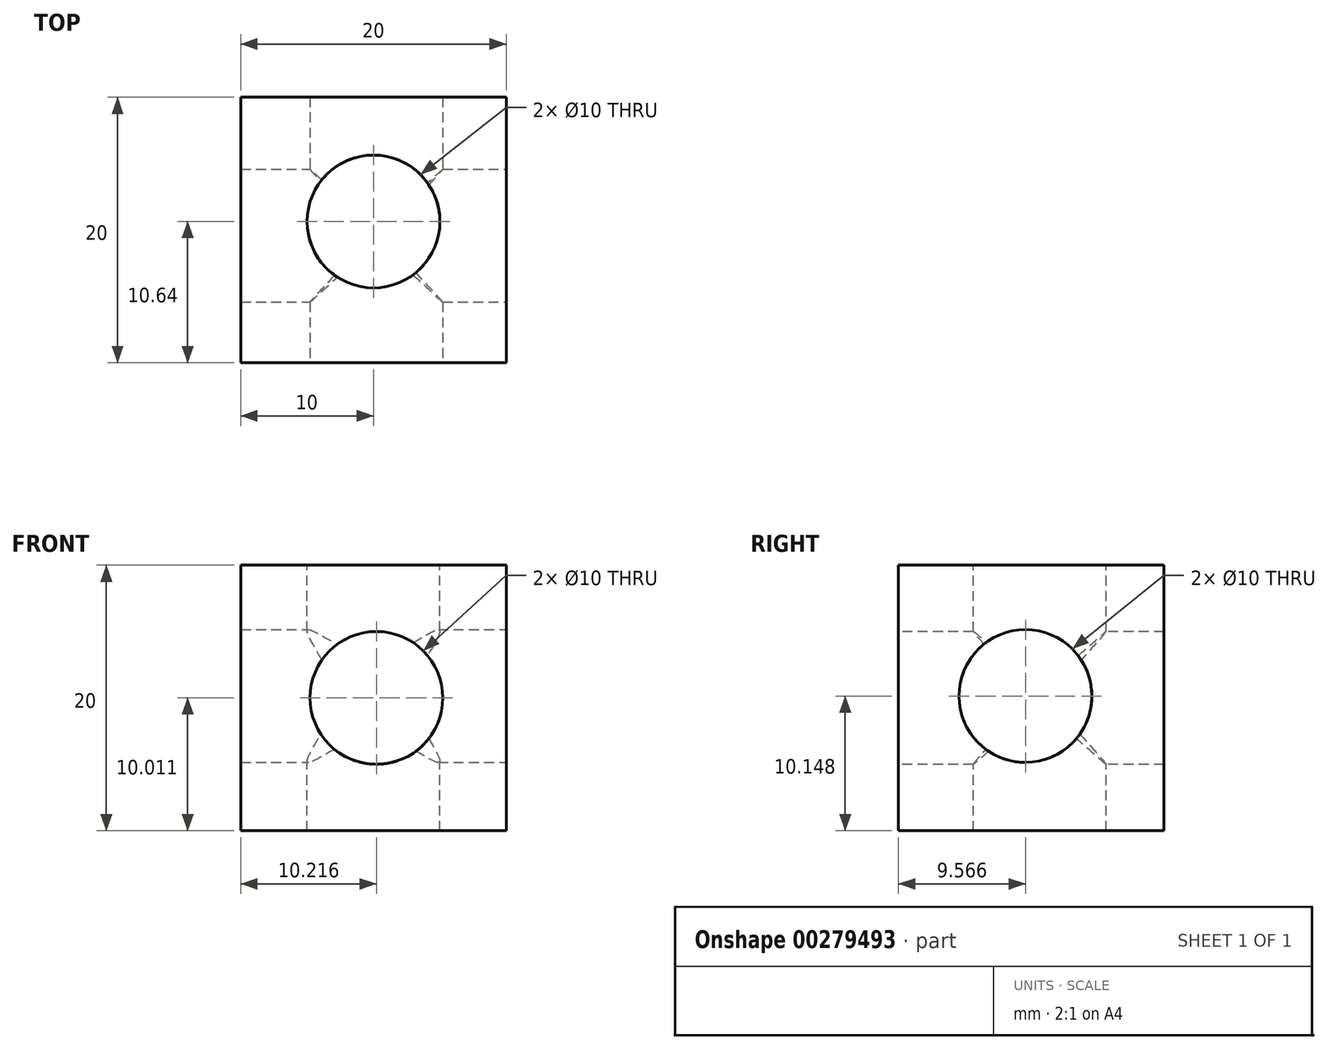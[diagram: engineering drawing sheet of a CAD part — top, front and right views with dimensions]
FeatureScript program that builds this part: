
annotation { "Feature Type Name" : "Feature", "Feature Type Description" : "" }
export const myFeature = defineFeature(function(context is Context, id is Id, definition is map)
    precondition{}
    {
        {
            var Q0;
            Q0=qCreatedBy(makeId("Top.planeOp"),FACE);
            var sketch = newSketch(context, id + "F0", { "sketchPlane" : qUnion([Q0])});
            skLineSegment(sketch, "E0.bottom", {"start": v(0, 20) * mm, "end": v(20, 20) * mm});
            skLineSegment(sketch, "E0.top", {"start": v(0, 0) * mm, "end": v(20, 0) * mm});
            skLineSegment(sketch, "E0.left", {"start": v(0, 20) * mm, "end": v(0, 0) * mm});
            skLineSegment(sketch, "E0.right", {"start": v(20, 20) * mm, "end": v(20, 0) * mm});
            skSolve(sketch);
        }
        {
            var Q0;
            Q0=makeQuery(id+"F0.imprint","IMPRINT",FACE,{"disambiguationData":[TD([[makeQuery(id+"F0.imprint","IMPRINT",EDGE,{"derivedFrom":sQuery(id+"F0.wireOp",EDGE,"E0.bottom")}),-1.0]])]});
            extrude(context, id + "F1", {"entities" : qUnion([Q0]), "depth" : 20 * mm});
        }
        {
            var Q0;
            Q0=qCreatedBy(makeId("Front.planeOp"),FACE);
            var sketch = newSketch(context, id + "F2", { "sketchPlane" : qUnion([Q0])});
            skCircle(sketch, "E1", {"center": v(10.22, 10.01) * mm, "radius": 5 * mm});
            skLineSegment(sketch, "E2", {"start": v(10.22, 20.02) * mm, "end": v(10.22, 0) * mm});
            skSolve(sketch);
        }
        {
            var Q0;
            Q0=makeQuery(id+"F2.imprint","IMPRINT",FACE,{"disambiguationData":[TD([[makeQuery(id+"F2.imprint","IMPRINT",EDGE,{"derivedFrom":sQuery(id+"F2.wireOp",EDGE,"E1")}),1.0]])]});
            extrude(context, id + "F3", {"entities" : qUnion([Q0]), "operationType" : NewBodyOperationType.REMOVE, "oppositeDirection" : true, "depth" : 20 * mm});
        }
        {
            var Q0;
            Q0=makeQuery(id+"F1.opExtrude","SWEPT_FACE",FACE,{"disambiguationData":[OSD([sQuery(id+"F0.wireOp",EDGE,"E0.right")])]});
            var sketch = newSketch(context, id + "F4", { "sketchPlane" : qUnion([Q0])});
            skCircle(sketch, "E3", {"center": v(9.57, 10.15) * mm, "radius": 5 * mm});
            skLineSegment(sketch, "E4", {"start": v(0, 10) * mm, "end": v(20, 10.15) * mm});
            skSolve(sketch);
        }
        {
            var Q0;
            {var subQ0=sQuery(id+"F4.wireOp",EDGE,"E4");var subQ1=sQuery(id+"F4.wireOp",EDGE,"E3");var subQ2=makeQuery(id+"F4.imprint","INTERSECT",VERTEX,{"disambiguationData":[OD(0.0)],"derivedFrom":[subQ1,subQ0]});Q0=makeQuery(id+"F4.imprint","IMPRINT",FACE,{"disambiguationData":[TD([[makeQuery(id+"F4.imprint","IMPRINT",EDGE,{"disambiguationData":[TD([[subQ2,1.0]])],"derivedFrom":subQ1}),1.0]])]});}
            var Q1;
            {var subQ0=sQuery(id+"F4.wireOp",EDGE,"E4");var subQ1=sQuery(id+"F4.wireOp",EDGE,"E3");var subQ2=makeQuery(id+"F4.imprint","INTERSECT",VERTEX,{"disambiguationData":[OD(0.0)],"derivedFrom":[subQ1,subQ0]});Q1=makeQuery(id+"F4.imprint","IMPRINT",FACE,{"disambiguationData":[TD([[makeQuery(id+"F4.imprint","IMPRINT",EDGE,{"disambiguationData":[TD([[subQ2,-1.0]])],"derivedFrom":subQ1}),1.0]])]});}
            var Q2;
            Q2=sQuery(id+"F4.wireOp",EDGE,"E3");
            extrude(context, id + "F5", {"entities" : qUnion([Q0, Q1]), "operationType" : NewBodyOperationType.REMOVE, "surfaceEntities" : qUnion([Q2]), "oppositeDirection" : true, "depth" : 20 * mm});
        }
        {
            var Q0;
            Q0=makeQuery(id+"F1.opExtrude","CAP_FACE",FACE,{"disambiguationData":[OSD([sQuery(id+"F0.wireOp",EDGE,"E0.bottom"),sQuery(id+"F0.wireOp",EDGE,"E0.top"),sQuery(id+"F0.wireOp",EDGE,"E0.left"),sQuery(id+"F0.wireOp",EDGE,"E0.right")])],"isStart":false});
            var sketch = newSketch(context, id + "F6", { "sketchPlane" : qUnion([Q0])});
            skCircle(sketch, "E5", {"center": v(10, 10.64) * mm, "radius": 5 * mm});
            skLineSegment(sketch, "E6", {"start": v(0, 10.64) * mm, "end": v(20, 10.64) * mm});
            skSolve(sketch);
        }
        {
            var Q0;
            {var subQ0=sQuery(id+"F6.wireOp",EDGE,"E6");var subQ1=sQuery(id+"F6.wireOp",EDGE,"E5");var subQ2=makeQuery(id+"F6.imprint","INTERSECT",VERTEX,{"disambiguationData":[OD(0.0)],"derivedFrom":[subQ1,subQ0]});Q0=makeQuery(id+"F6.imprint","IMPRINT",FACE,{"disambiguationData":[TD([[makeQuery(id+"F6.imprint","IMPRINT",EDGE,{"disambiguationData":[TD([[subQ2,1.0]])],"derivedFrom":subQ1}),1.0]])]});}
            var Q1;
            {var subQ0=sQuery(id+"F6.wireOp",EDGE,"E6");var subQ1=sQuery(id+"F6.wireOp",EDGE,"E5");var subQ2=makeQuery(id+"F6.imprint","INTERSECT",VERTEX,{"disambiguationData":[OD(0.0)],"derivedFrom":[subQ1,subQ0]});Q1=makeQuery(id+"F6.imprint","IMPRINT",FACE,{"disambiguationData":[TD([[makeQuery(id+"F6.imprint","IMPRINT",EDGE,{"disambiguationData":[TD([[subQ2,-1.0]])],"derivedFrom":subQ1}),1.0]])]});}
            var Q2;
            Q2=sQuery(id+"F6.wireOp",EDGE,"E5");
            extrude(context, id + "F7", {"entities" : qUnion([Q0, Q1]), "operationType" : NewBodyOperationType.REMOVE, "surfaceEntities" : qUnion([Q2]), "oppositeDirection" : true, "depth" : 20 * mm});
        }
    });
